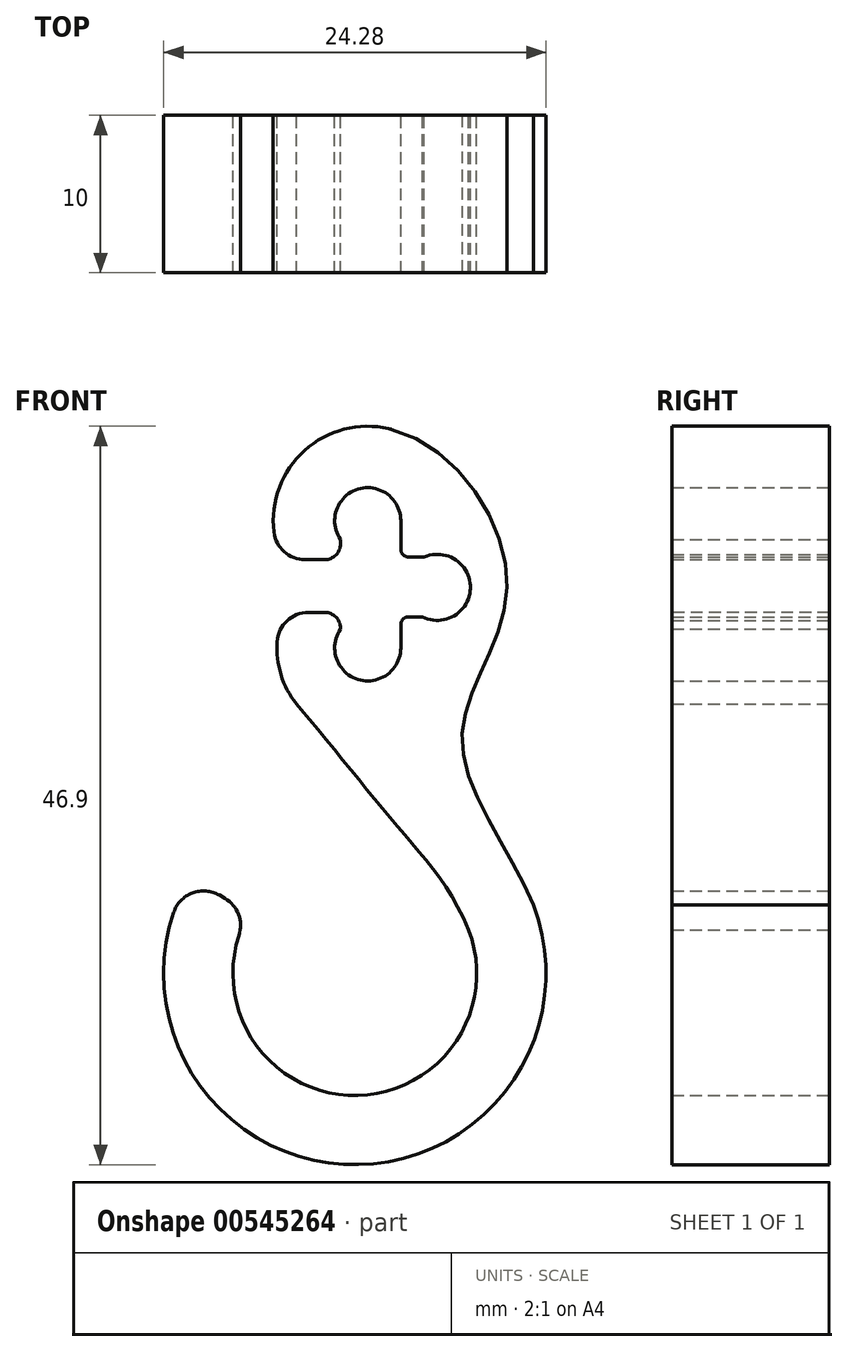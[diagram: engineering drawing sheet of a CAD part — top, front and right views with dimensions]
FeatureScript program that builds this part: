
annotation { "Feature Type Name" : "Feature", "Feature Type Description" : "" }
export const myFeature = defineFeature(function(context is Context, id is Id, definition is map)
    precondition{}
    {
        {
            var Q0;
            Q0=qCreatedBy(makeId("Front.planeOp"),FACE);
            var sketch = newSketch(context, id + "F0", { "sketchPlane" : qUnion([Q0])});
            skCircle(sketch, "E0", {"center": v(0, 0) * mm, "radius": 2.1 * mm});
            skCircle(sketch, "E1", {"center": v(0, -8.07) * mm, "radius": 2.1 * mm});
            skLineSegment(sketch, "E2", {"start": v(2.1, 0) * mm, "end": v(2.1, -8.07) * mm});
            skArc(sketch, "E3", {"start": v(5.47, -2.47) * mm, "mid": v(0, 6) * mm, "end": v(-5.47, -2.47) * mm});
            skArc(sketch, "E4", {"start": v(-5.31, -5.82) * mm, "mid": v(-0.06, -13.84) * mm, "end": v(5.36, -5.94) * mm});
            skLineSegment(sketch, "E5", {"start": v(-5.31, -5.82) * mm, "end": v(-1.73, -5.82) * mm});
            skLineSegment(sketch, "E6", {"start": v(-5.47, -2.47) * mm, "end": v(-1.73, -2.47) * mm});
            skLineSegment(sketch, "E7", {"start": v(-1.73, -2.47) * mm, "end": v(-1.73, -1.2) * mm});
            skLineSegment(sketch, "E8", {"start": v(-1.73, -5.82) * mm, "end": v(-1.73, -6.88) * mm});
            skArc(sketch, "E9", {"start": v(-11.33, -22.68) * mm, "mid": v(-1.78, -40.86) * mm, "end": v(10.52, -24.41) * mm});
            skArc(sketch, "E10.0", {"start": v(-7.52, -24.88) * mm, "mid": v(-1.43, -36.47) * mm, "end": v(6.41, -25.99) * mm});
            skFitSpline(sketch, "E11", {"points": [v(-4.53, -11.65) * mm, v(1.8, -19.3) * mm, v(6.41, -25.99) * mm], "startDerivative": vector(12.67, -14.72) * mm, "endDerivative": vector(7.73, -18.47) * mm});
            skLineSegment(sketch, "E12", {"start": v(-11.33, -22.68) * mm, "end": v(-7.52, -24.88) * mm});
            skCircle(sketch, "E13", {"center": v(4.42, -4.23) * mm, "radius": 2.1 * mm});
            skFitSpline(sketch, "E14", {"points": [v(1.34, 5.85) * mm, v(8.85, -4.24) * mm, v(5.98, -13.83) * mm, v(10.52, -24.41) * mm], "startDerivative": vector(37.27, -8.61) * mm, "endDerivative": vector(12.03, -29.95) * mm});
            skLineSegment(sketch, "E15", {"start": v(2.1, -6.1) * mm, "end": v(3.47, -6.1) * mm});
            skLineSegment(sketch, "E16", {"start": v(2.1, -2.3) * mm, "end": v(3.59, -2.3) * mm});
            skSolve(sketch);
        }
        {
            var Q0;
            Q0=makeQuery(id+"F0.imprint","IMPRINT",FACE,{"disambiguationData":[TD([[makeQuery(id+"F0.imprint","IMPRINT",EDGE,{"derivedFrom":sQuery(id+"F0.wireOp",EDGE,"E9")}),1.0]])]});
            var Q1;
            {var subQ5=sQuery(id+"F0.wireOp",EDGE,"E6");Q1=makeQuery(id+"F0.imprint","IMPRINT",FACE,{"disambiguationData":[TD([[makeQuery(id+"F0.imprint","IMPRINT",EDGE,{"derivedFrom":subQ5}),1.0]])]});}
            var Q2;
            {var subQ5=sQuery(id+"F0.wireOp",EDGE,"E5");Q2=makeQuery(id+"F0.imprint","IMPRINT",FACE,{"disambiguationData":[TD([[makeQuery(id+"F0.imprint","IMPRINT",EDGE,{"derivedFrom":subQ5}),-1.0]])]});}
            extrude(context, id + "F1", {"entities" : qUnion([Q0, Q1, Q2]), "depth" : 10 * mm, "offsetDistance" : 25 * mm});
        }
        {
            var Q0;
            Q0=makeQuery(id+"F1.opExtrude","SWEPT_EDGE",EDGE,{"disambiguationData":[OSD([sQuery(id+"F0.wireOp",EDGE,"E6"),sQuery(id+"F0.wireOp",EDGE,"E7")])]});
            var Q1;
            Q1=makeQuery(id+"F1.opExtrude","SWEPT_EDGE",EDGE,{"disambiguationData":[OSD([sQuery(id+"F0.wireOp",EDGE,"E5"),sQuery(id+"F0.wireOp",EDGE,"E8")])]});
            fillet(context, id + "F2", {"entities" : qUnion([Q0, Q1]), "radius" : 1 * mm, "tangentPropagation" : true, "allowEdgeOverflow" : false});
        }
        {
            var Q0;
            Q0=makeQuery(id+"F1.opExtrude","SWEPT_EDGE",EDGE,{"disambiguationData":[OSD([sQuery(id+"F0.wireOp",EDGE,"E9"),sQuery(id+"F0.wireOp",EDGE,"E12")])]});
            var Q1;
            Q1=makeQuery(id+"F1.opExtrude","SWEPT_EDGE",EDGE,{"disambiguationData":[OSD([sQuery(id+"F0.wireOp",EDGE,"E10.0"),sQuery(id+"F0.wireOp",EDGE,"E12")])]});
            var Q2;
            Q2=makeQuery(id+"F1.opExtrude","SWEPT_EDGE",EDGE,{"disambiguationData":[OSD([sQuery(id+"F0.wireOp",EDGE,"E3"),sQuery(id+"F0.wireOp",EDGE,"E6")])]});
            var Q3;
            Q3=makeQuery(id+"F1.opExtrude","SWEPT_EDGE",EDGE,{"disambiguationData":[OSD([sQuery(id+"F0.wireOp",EDGE,"E4"),sQuery(id+"F0.wireOp",EDGE,"E5")])]});
            fillet(context, id + "F3", {"entities" : qUnion([Q0, Q1, Q2, Q3]), "radius" : 2 * mm, "tangentPropagation" : true, "allowEdgeOverflow" : false});
        }
        {
            var Q0;
            Q0=makeQuery(id+"F1.opExtrude","SWEPT_EDGE",EDGE,{"disambiguationData":[OSD([sQuery(id+"F0.wireOp",EDGE,"E2"),sQuery(id+"F0.wireOp",EDGE,"E16")])]});
            var Q1;
            Q1=makeQuery(id+"F1.opExtrude","SWEPT_EDGE",EDGE,{"disambiguationData":[OSD([sQuery(id+"F0.wireOp",EDGE,"E2"),sQuery(id+"F0.wireOp",EDGE,"E15")])]});
            fillet(context, id + "F4", {"entities" : qUnion([Q0, Q1]), "radius" : 0.5 * mm, "tangentPropagation" : true, "allowEdgeOverflow" : false});
        }
    });
